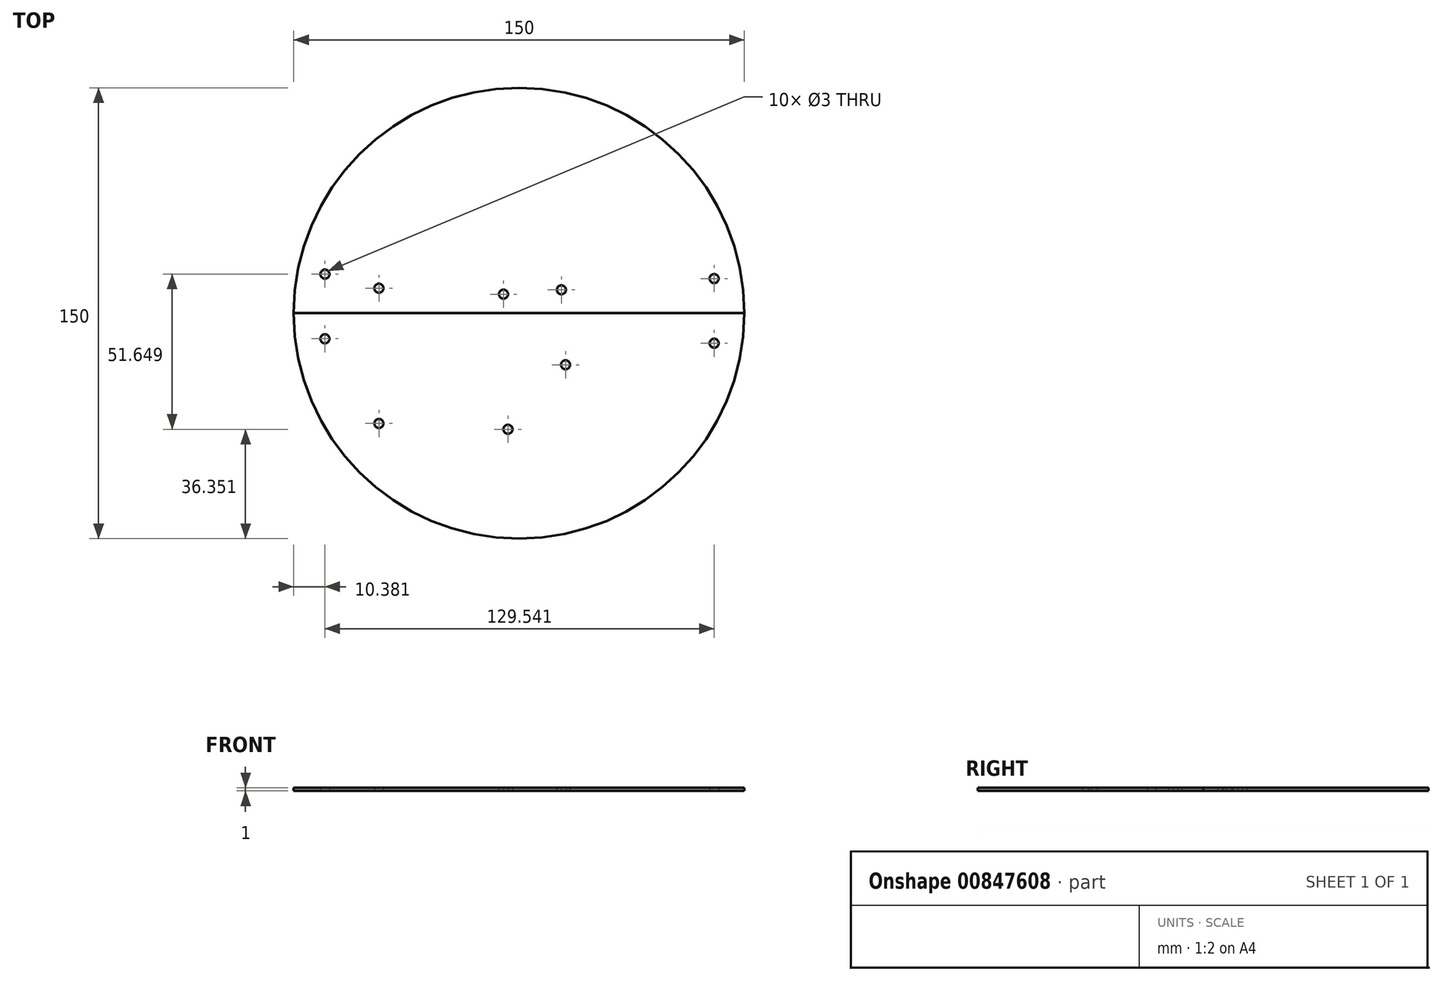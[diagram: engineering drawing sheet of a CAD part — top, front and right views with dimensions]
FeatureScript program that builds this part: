
annotation { "Feature Type Name" : "Feature", "Feature Type Description" : "" }
export const myFeature = defineFeature(function(context is Context, id is Id, definition is map)
    precondition{}
    {
        {
            var Q0;
            Q0=qCreatedBy(makeId("Top.planeOp"),FACE);
            var sketch = newSketch(context, id + "F0", { "sketchPlane" : qUnion([Q0])});
            skCircle(sketch, "E0", {"center": v(0, 0) * mm, "radius": 75 * mm});
            skLineSegment(sketch, "E1", {"start": v(0, 0) * mm, "end": v(75, 0) * mm});
            skLineSegment(sketch, "E2", {"start": v(0, 0) * mm, "end": v(-75, 0) * mm});
            skSolve(sketch);
        }
        {
            var Q0;
            {var subQ0=sQuery(id+"F0.wireOp",EDGE,"E1");Q0=makeQuery(id+"F0.imprint","IMPRINT",FACE,{"disambiguationData":[TD([[makeQuery(id+"F0.imprint","IMPRINT",EDGE,{"derivedFrom":subQ0}),1.0]])]});}
            var sketch = newSketch(context, id + "F1", { "sketchPlane" : qUnion([Q0])});
            skCircle(sketch, "E3", {"center": v(64.92, 11.5) * mm, "radius": 1.5 * mm});
            skCircle(sketch, "E4", {"center": v(64.92, -10) * mm, "radius": 1.5 * mm});
            skSolve(sketch);
        }
        {
            var Q0;
            {var subQ0=sQuery(id+"F0.wireOp",EDGE,"E1");Q0=makeQuery(id+"F0.imprint","IMPRINT",FACE,{"disambiguationData":[TD([[makeQuery(id+"F0.imprint","IMPRINT",EDGE,{"derivedFrom":subQ0}),1.0]])]});}
            var sketch = newSketch(context, id + "F2", { "sketchPlane" : qUnion([Q0])});
            skCircle(sketch, "E5", {"center": v(-64.62, 13) * mm, "radius": 1.5 * mm});
            skCircle(sketch, "E6", {"center": v(-64.62, -8.5) * mm, "radius": 1.5 * mm});
            skSolve(sketch);
        }
        {
            var Q0;
            Q0=makeQuery(id+"F1.imprint","IMPRINT",FACE,{"disambiguationData":[TD([[makeQuery(id+"F1.imprint","IMPRINT",EDGE,{"derivedFrom":sQuery(id+"F1.wireOp",EDGE,"E3")}),-1.0]])]});
            var sketch = newSketch(context, id + "F3", { "sketchPlane" : qUnion([Q0])});
            skCircle(sketch, "E7", {"center": v(14.1, 7.78) * mm, "radius": 1.5 * mm});
            skCircle(sketch, "E8", {"center": v(15.47, -17.18) * mm, "radius": 1.5 * mm});
            skSolve(sketch);
        }
        {
            var Q0;
            {var subQ0=sQuery(id+"F0.wireOp",EDGE,"E1");Q0=makeQuery(id+"F0.imprint","IMPRINT",FACE,{"disambiguationData":[TD([[makeQuery(id+"F0.imprint","IMPRINT",EDGE,{"derivedFrom":subQ0}),1.0]])]});}
            var sketch = newSketch(context, id + "F4", { "sketchPlane" : qUnion([Q0])});
            skCircle(sketch, "E9", {"center": v(-46.64, 8.3) * mm, "radius": 1.5 * mm});
            skCircle(sketch, "E10", {"center": v(-5.2, 6.33) * mm, "radius": 1.5 * mm});
            skCircle(sketch, "E11", {"center": v(-46.64, -36.7) * mm, "radius": 1.5 * mm});
            skCircle(sketch, "E12", {"center": v(-3.69, -38.65) * mm, "radius": 1.5 * mm});
            skSolve(sketch);
        }
        {
            var Q0;
            {var subQ0=sQuery(id+"F0.wireOp",EDGE,"E1");Q0=makeQuery(id+"F0.imprint","IMPRINT",FACE,{"disambiguationData":[TD([[makeQuery(id+"F0.imprint","IMPRINT",EDGE,{"derivedFrom":subQ0}),-1.0]])]});}
            var Q1;
            Q1=makeQuery(id+"F1.imprint","IMPRINT",FACE,{"disambiguationData":[TD([[makeQuery(id+"F1.imprint","IMPRINT",EDGE,{"derivedFrom":sQuery(id+"F1.wireOp",EDGE,"E3")}),-1.0]])]});
            extrude(context, id + "F5", {"entities" : qUnion([Q0, Q1]), "depth" : 1 * mm, "offsetDistance" : 25 * mm});
        }
        {
            var Q0;
            Q0 = qSketchRegion(id + "F3", true);
            var Q1;
            Q1 = qSketchRegion(id + "F4", true);
            var Q2;
            Q2 = qSketchRegion(id + "F2", true);
            extrude(context, id + "F6", {"entities" : qUnion([Q0, Q1, Q2]), "operationType" : NewBodyOperationType.REMOVE, "depth" : 5 * mm, "offsetDistance" : 25 * mm});
        }
        {
            var Q0;
            Q0 = qSketchRegion(id + "F1", true);
            extrude(context, id + "F7", {"entities" : qUnion([Q0]), "operationType" : NewBodyOperationType.REMOVE, "depth" : 25 * mm, "offsetDistance" : 25 * mm});
        }
    });
